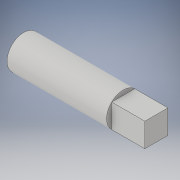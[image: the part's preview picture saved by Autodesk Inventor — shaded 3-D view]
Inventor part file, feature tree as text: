
AUTODESK INVENTOR PART (.ipt)
format: ipt  version: 2019 (Build 230136000, 136)  size: 105,984 bytes
history: native  units: in
note: dims shown in document units (in); Inventor stores cm internally (conversion verified against a paired STEP export)
features: other x3, extrude x1, sketch x1
ambient origin geometry x8: Origin, YZ Plane, XZ Plane, XY Plane, X Axis, Y Axis, Z Axis, Center Point
bodies: Solid1 (feature_tree)
feature tree (5):
  other  "SkeletalStuff.ipt"
  extrude  "Extrusion1"  Depth=0.5in TaperAngle=0.0deg
  other  "Solid2::SkeletalStuff.ipt"
  other  "TaggingFeature1"
  sketch  "Sketch1"  dims[d0=0.3937in d1=0.5in d2=0.0in]
